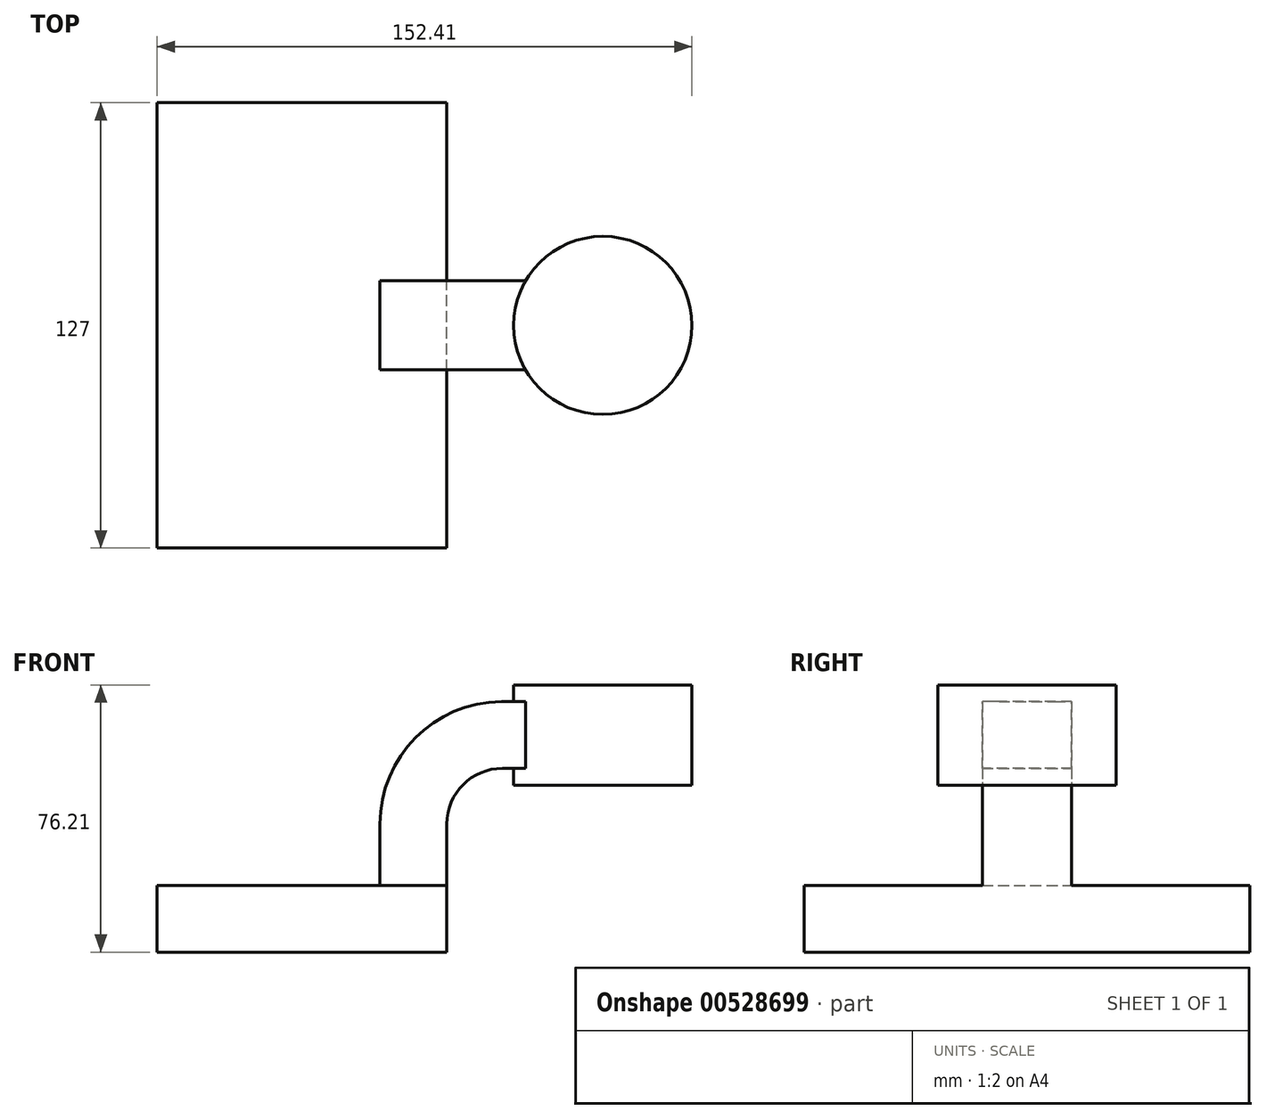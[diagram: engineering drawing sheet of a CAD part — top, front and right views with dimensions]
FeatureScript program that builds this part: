
annotation { "Feature Type Name" : "Feature", "Feature Type Description" : "" }
export const myFeature = defineFeature(function(context is Context, id is Id, definition is map)
    precondition{}
    {
        {
            var Q0;
            Q0=qCreatedBy(makeId("Front.planeOp"),FACE);
            var sketch = newSketch(context, id + "F0", { "sketchPlane" : qUnion([Q0])});
            skLineSegment(sketch, "E0.bottom", {"start": v(41.27, 9.53) * mm, "end": v(-41.28, 9.53) * mm});
            skLineSegment(sketch, "E0.top", {"start": v(41.28, -9.52) * mm, "end": v(-41.27, -9.52) * mm});
            skLineSegment(sketch, "E0.left", {"start": v(41.28, 9.53) * mm, "end": v(41.28, -9.52) * mm});
            skLineSegment(sketch, "E0.right", {"start": v(-41.28, 9.53) * mm, "end": v(-41.27, -9.52) * mm});
            skPoint(sketch, "E0.middle", {"position": v(0, 0) * mm});
            skLineSegment(sketch, "E1.bottom", {"start": v(111.13, 38.1) * mm, "end": v(60.33, 38.1) * mm});
            skLineSegment(sketch, "E1.top", {"start": v(111.12, 66.68) * mm, "end": v(60.33, 66.68) * mm});
            skLineSegment(sketch, "E1.left", {"start": v(111.13, 38.1) * mm, "end": v(111.12, 66.68) * mm});
            skLineSegment(sketch, "E1.right", {"start": v(60.33, 38.1) * mm, "end": v(60.33, 66.68) * mm});
            skPoint(sketch, "E1.middle", {"position": v(85.73, 52.39) * mm});
            skLineSegment(sketch, "E2", {"start": v(41.27, 9.53) * mm, "end": v(41.27, 27) * mm});
            skArc(sketch, "E3", {"start": v(41.27, 27) * mm, "mid": v(45.92, 38.23) * mm, "end": v(57.15, 42.88) * mm});
            skLineSegment(sketch, "E4", {"start": v(57.15, 42.88) * mm, "end": v(85.73, 42.88) * mm});
            skLineSegment(sketch, "E5.0", {"start": v(57.15, 61.93) * mm, "end": v(85.73, 61.93) * mm});
            skArc(sketch, "E5.1", {"start": v(22.22, 27) * mm, "mid": v(32.45, 51.7) * mm, "end": v(57.15, 61.93) * mm});
            skLineSegment(sketch, "E5.2", {"start": v(22.22, 9.53) * mm, "end": v(22.22, 27) * mm});
            skFitSpline(sketch, "E6", {"points": [v(57.15, 61.93) * mm, v(-41.27, 9.52) * mm], "startDerivative": vector(-132.02, -0.5) * mm, "endDerivative": vector(0.11, -101.27) * mm});
            skLineSegment(sketch, "E7", {"start": v(85.73, 66.68) * mm, "end": v(85.73, 38.1) * mm});
            skSolve(sketch);
        }
        {
            var Q0;
            Q0=makeQuery(id+"F0.imprint","IMPRINT",FACE,{"disambiguationData":[TD([[makeQuery(id+"F0.imprint","IMPRINT",EDGE,{"derivedFrom":sQuery(id+"F0.wireOp",EDGE,"E0.top")}),-1.0]])]});
            extrude(context, id + "F1", {"entities" : qUnion([Q0]), "endBound" : BoundingType.SYMMETRIC, "depth" : 127 * mm, "offsetDistance" : 25.4 * mm});
        }
        {
            var Q0;
            {var subQ1=sQuery(id+"F0.wireOp",EDGE,"E2");Q0=makeQuery(id+"F0.imprint","IMPRINT",FACE,{"disambiguationData":[TD([[makeQuery(id+"F0.imprint","IMPRINT",EDGE,{"derivedFrom":subQ1}),1.0]])]});}
            var Q1;
            {var subQ0=sQuery(id+"F0.wireOp",EDGE,"E4");var subQ1=sQuery(id+"F0.wireOp",EDGE,"E1.right");var subQ2=makeQuery(id+"F0.imprint","INTERSECT",VERTEX,{"derivedFrom":[subQ1,subQ0]});Q1=makeQuery(id+"F0.imprint","IMPRINT",FACE,{"disambiguationData":[TD([[makeQuery(id+"F0.imprint","IMPRINT",EDGE,{"disambiguationData":[TD([[subQ2,-1.0]])],"derivedFrom":subQ1}),-1.0]])]});}
            extrude(context, id + "F2", {"entities" : qUnion([Q0, Q1]), "operationType" : NewBodyOperationType.ADD, "endBound" : BoundingType.SYMMETRIC, "depth" : 25.4 * mm, "offsetDistance" : 25.4 * mm});
        }
        {
            var Q0;
            {var subQ4=sQuery(id+"F0.wireOp",EDGE,"E5.1");Q0=makeQuery(id+"F0.imprint","IMPRINT",FACE,{"disambiguationData":[TD([[makeQuery(id+"F0.imprint","IMPRINT",EDGE,{"derivedFrom":subQ4}),1.0]])]});}
            extrude(context, id + "F3", {"entities" : qUnion([Q0]), "operationType" : NewBodyOperationType.ADD, "endBound" : BoundingType.SYMMETRIC, "depth" : 15.88 * mm, "offsetDistance" : 25.4 * mm});
        }
        {
            var Q0;
            {var subQ4=sQuery(id+"F0.wireOp",EDGE,"E1.left");Q0=makeQuery(id+"F0.imprint","IMPRINT",FACE,{"disambiguationData":[TD([[makeQuery(id+"F0.imprint","IMPRINT",EDGE,{"derivedFrom":subQ4}),1.0]])]});}
            var Q1;
            Q1=sQuery(id+"F0.wireOp",EDGE,"E7");
            revolve(context, id + "F4", {"operationType" : NewBodyOperationType.ADD, "surfaceOperationType" : NewSurfaceOperationType.NEW, "entities" : qUnion([Q0]), "axis" : qUnion([Q1]), "revolveType" : RevolveType.FULL});
        }
    });
